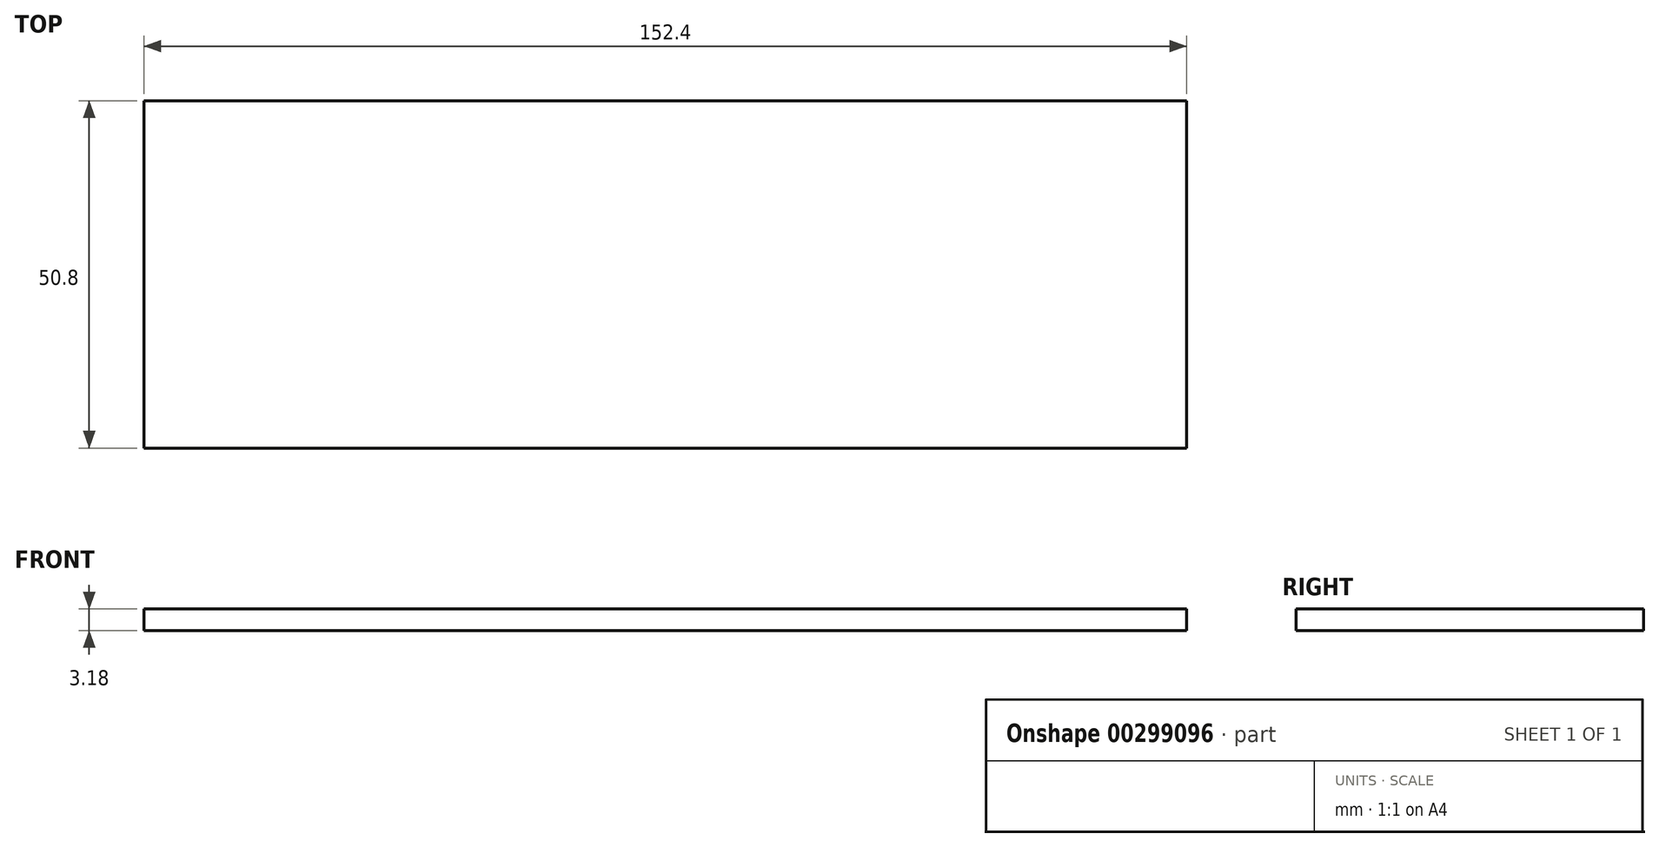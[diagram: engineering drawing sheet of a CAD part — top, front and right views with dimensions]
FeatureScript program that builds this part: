
annotation { "Feature Type Name" : "Feature", "Feature Type Description" : "" }
export const myFeature = defineFeature(function(context is Context, id is Id, definition is map)
    precondition{}
    {
        {
            var Q0;
            Q0=qCreatedBy(makeId("Top.planeOp"),FACE);
            var sketch = newSketch(context, id + "F0", { "sketchPlane" : qUnion([Q0])});
            skLineSegment(sketch, "E0.bottom", {"start": v(-76.2, 25.4) * mm, "end": v(76.2, 25.4) * mm});
            skLineSegment(sketch, "E0.top", {"start": v(-76.2, -25.4) * mm, "end": v(76.2, -25.4) * mm});
            skLineSegment(sketch, "E0.left", {"start": v(-76.2, 25.4) * mm, "end": v(-76.2, -25.4) * mm});
            skLineSegment(sketch, "E0.right", {"start": v(76.2, 25.4) * mm, "end": v(76.2, -25.4) * mm});
            skPoint(sketch, "E0.middle", {"position": v(0, 0) * mm});
            skSolve(sketch);
        }
        {
            var Q0;
            Q0 = qSketchRegion(id + "F0", true);
            extrude(context, id + "F1", {"entities" : qUnion([Q0]), "endBound" : BoundingType.SYMMETRIC, "depth" : 3.17 * mm});
        }
    });
